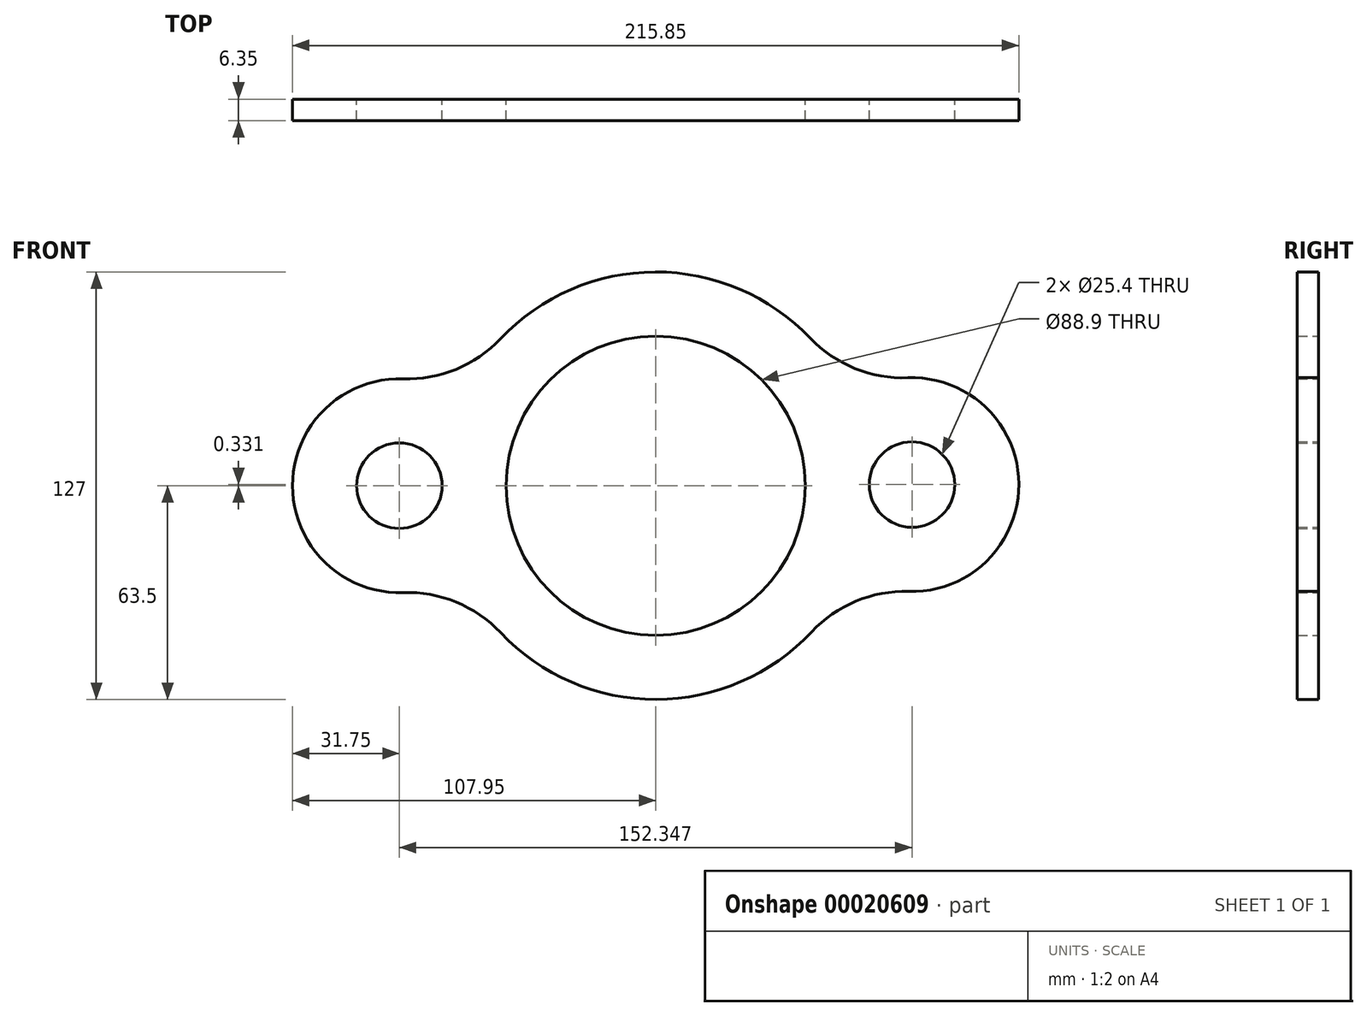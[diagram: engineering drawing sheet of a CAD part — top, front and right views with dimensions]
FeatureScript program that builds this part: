
annotation { "Feature Type Name" : "Feature", "Feature Type Description" : "" }
export const myFeature = defineFeature(function(context is Context, id is Id, definition is map)
    precondition{}
    {
        {
            var Q0;
            Q0=qCreatedBy(makeId("Front.planeOp"),FACE);
            var sketch = newSketch(context, id + "F0", { "sketchPlane" : qUnion([Q0])});
            skCircle(sketch, "E0", {"center": v(0, 0) * mm, "radius": 44.45 * mm});
            skArc(sketch, "E1", {"start": v(-46.14, -43.63) * mm, "mid": v(0.14, -63.5) * mm, "end": v(46.32, -43.43) * mm});
            skArc(sketch, "E2", {"start": v(-75.12, 31.73) * mm, "mid": v(-107.95, 0) * mm, "end": v(-75.12, -31.73) * mm});
            skArc(sketch, "E3", {"start": v(44.42, 1.58) * mm, "mid": v(44.4, 0.2) * mm, "end": v(44.43, -1.2) * mm});
            skCircle(sketch, "E4", {"center": v(-76.2, 0) * mm, "radius": 12.7 * mm});
            skCircle(sketch, "E5", {"center": v(76.15, 0.33) * mm, "radius": 12.7 * mm});
            skArc(sketch, "E6.trimOffspring", {"start": v(75.23, -31.4) * mm, "mid": v(107.9, 0.47) * mm, "end": v(74.95, 32.06) * mm});
            skArc(sketch, "E7.trimOffspring", {"start": v(45.95, 43.83) * mm, "mid": v(-0.14, 63.5) * mm, "end": v(-46.14, 43.63) * mm});
            skArc(sketch, "E8.trimOffspring", {"start": v(63.5, -0.77) * mm, "mid": v(63.5, 0.28) * mm, "end": v(63.49, 1.32) * mm});
            skPoint(sketch, "E9.visualSharp", {"position": v(-57.94, 25.98) * mm});
            skArc(sketch, "E9.filletArc", {"start": v(-75.12, 31.73) * mm, "mid": v(-59.35, 34.56) * mm, "end": v(-46.14, 43.63) * mm});
            skPoint(sketch, "E10.visualSharp", {"position": v(-57.94, -25.98) * mm});
            skArc(sketch, "E10.filletArc", {"start": v(-46.14, -43.63) * mm, "mid": v(-59.35, -34.56) * mm, "end": v(-75.12, -31.73) * mm});
            skPoint(sketch, "E11.visualSharp", {"position": v(57.82, 26.26) * mm});
            skArc(sketch, "E11.filletArc", {"start": v(45.95, 43.83) * mm, "mid": v(59.18, 34.83) * mm, "end": v(74.95, 32.06) * mm});
            skPoint(sketch, "E12.visualSharp", {"position": v(58.04, -25.75) * mm});
            skArc(sketch, "E12.filletArc", {"start": v(75.23, -31.4) * mm, "mid": v(59.48, -34.31) * mm, "end": v(46.32, -43.43) * mm});
            skSolve(sketch);
        }
        {
            var Q0;
            Q0=makeQuery(id+"F0.imprint","IMPRINT",FACE,{"disambiguationData":[TD([[makeQuery(id+"F0.imprint","IMPRINT",EDGE,{"derivedFrom":sQuery(id+"F0.wireOp",EDGE,"E1")}),1.0]])]});
            extrude(context, id + "F1", {"entities" : qUnion([Q0]), "depth" : 6.35 * mm});
        }
    });
